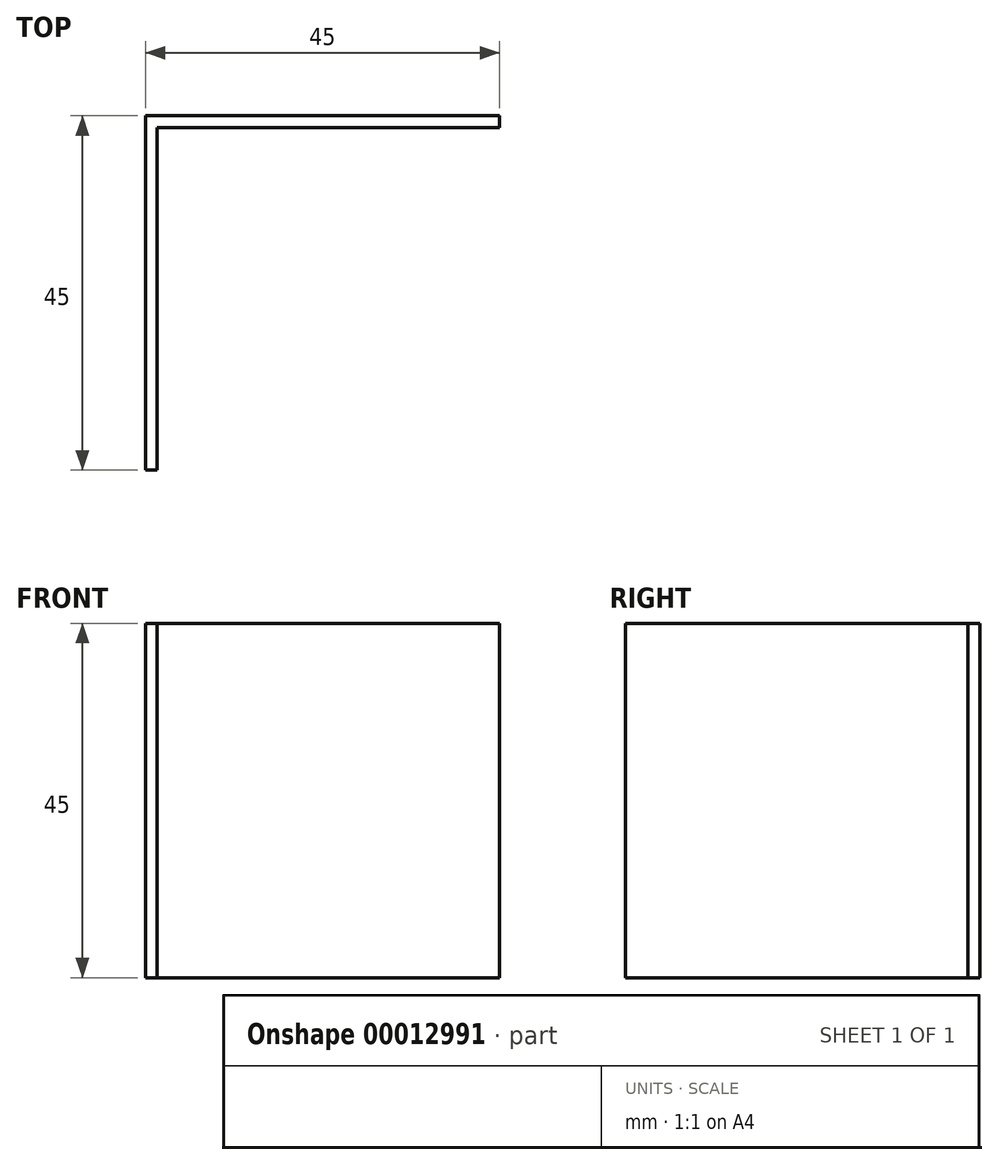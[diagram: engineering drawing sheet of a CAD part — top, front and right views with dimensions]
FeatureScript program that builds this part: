
annotation { "Feature Type Name" : "Feature", "Feature Type Description" : "" }
export const myFeature = defineFeature(function(context is Context, id is Id, definition is map)
    precondition{}
    {
        {
            var Q0;
            Q0=qCreatedBy(makeId("Top.planeOp"),FACE);
            var sketch = newSketch(context, id + "F0", { "sketchPlane" : qUnion([Q0])});
            skLineSegment(sketch, "E0.bottom", {"start": v(0, 0) * mm, "end": v(45, 0) * mm});
            skLineSegment(sketch, "E1", {"start": v(0, 0) * mm, "end": v(0, -45) * mm});
            skLineSegment(sketch, "E2", {"start": v(0, -45) * mm, "end": v(1.5, -45) * mm});
            skLineSegment(sketch, "E3", {"start": v(1.5, -45) * mm, "end": v(1.5, -1.5) * mm});
            skLineSegment(sketch, "E4", {"start": v(1.5, -1.5) * mm, "end": v(45, -1.5) * mm});
            skLineSegment(sketch, "E5", {"start": v(45, -1.5) * mm, "end": v(45, 0) * mm});
            skSolve(sketch);
        }
        {
            var Q0;
            Q0=makeQuery(id+"F0.imprint","IMPRINT",FACE,{"disambiguationData":[TD([[makeQuery(id+"F0.imprint","IMPRINT",EDGE,{"derivedFrom":sQuery(id+"F0.wireOp",EDGE,"E0.bottom")}),-1.0]])]});
            extrude(context, id + "F1", {"entities" : qUnion([Q0]), "depth" : 45 * mm});
        }
    });
